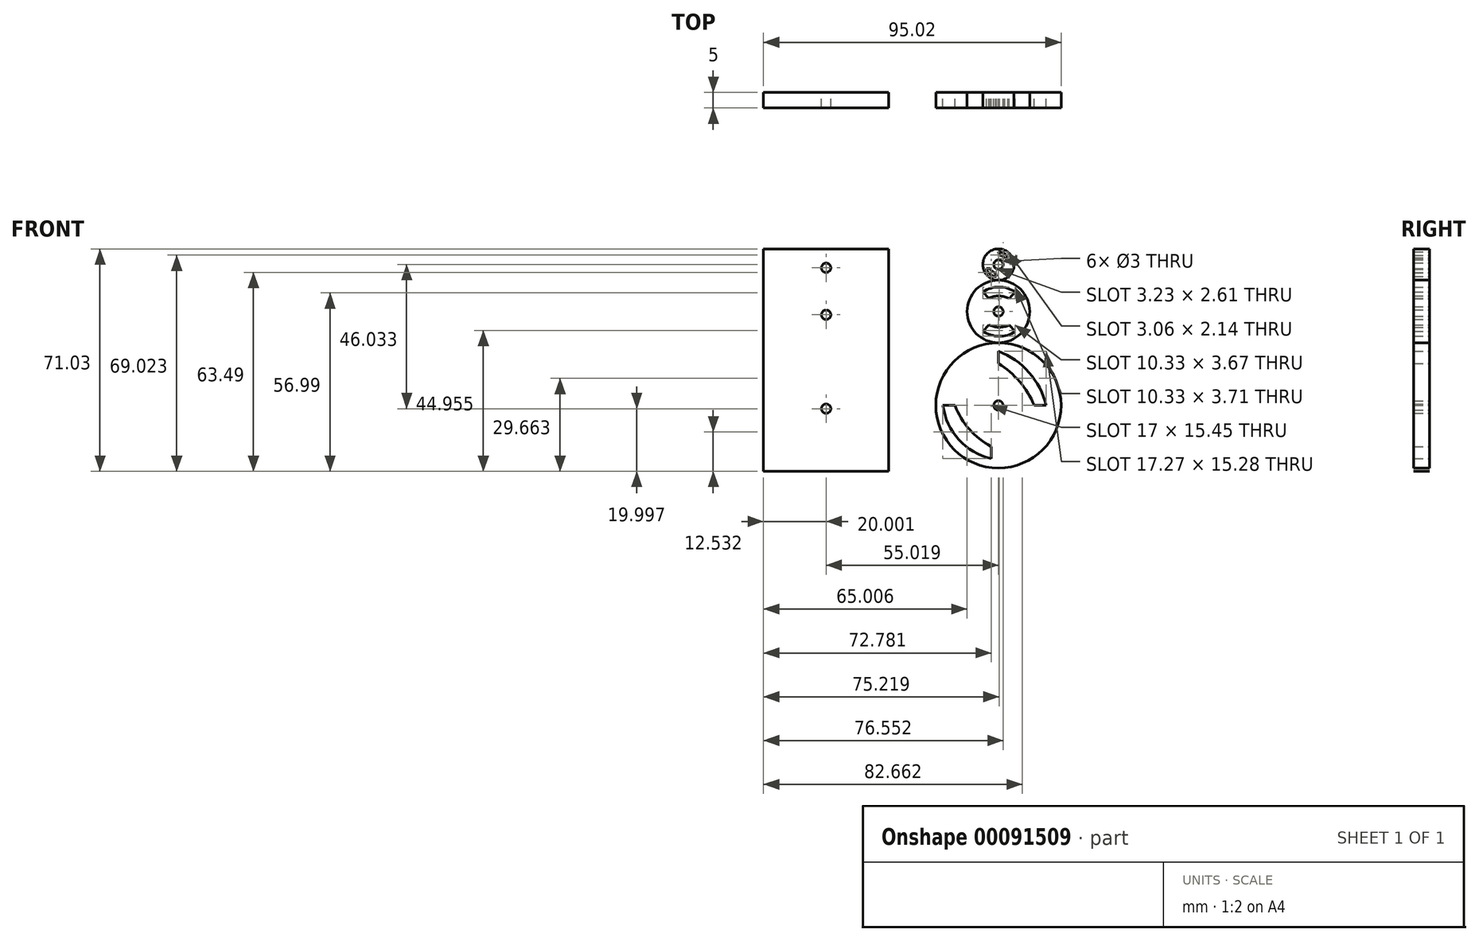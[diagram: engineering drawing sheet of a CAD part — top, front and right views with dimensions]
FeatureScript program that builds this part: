
annotation { "Feature Type Name" : "Feature", "Feature Type Description" : "" }
export const myFeature = defineFeature(function(context is Context, id is Id, definition is map)
    precondition{}
    {
        {
            var Q0;
            Q0=qCreatedBy(makeId("Front.planeOp"),FACE);
            var sketch = newSketch(context, id + "F0", { "sketchPlane" : qUnion([Q0])});
            skCircle(sketch, "E0", {"center": v(0, 0) * mm, "radius": 20 * mm});
            skCircle(sketch, "E1", {"center": v(0, 30) * mm, "radius": 10 * mm});
            skCircle(sketch, "E2", {"center": v(0, 0) * mm, "radius": 1.5 * mm});
            skCircle(sketch, "E3", {"center": v(0, 30) * mm, "radius": 1.5 * mm});
            skLineSegment(sketch, "E4", {"start": v(0, -20) * mm, "end": v(-20, -20) * mm});
            skLineSegment(sketch, "E5", {"start": v(0, -20) * mm, "end": v(20, -20) * mm});
            skCircle(sketch, "E6", {"center": v(0, 45) * mm, "radius": 5 * mm});
            skCircle(sketch, "E7", {"center": v(0, 45) * mm, "radius": 1.5 * mm});
            skLineSegment(sketch, "E8", {"start": v(20, -20) * mm, "end": v(20, 51) * mm});
            skLineSegment(sketch, "E9", {"start": v(20, 51) * mm, "end": v(20, 44.98) * mm});
            skLineSegment(sketch, "E10", {"start": v(-20, -20) * mm, "end": v(-20, 51) * mm});
            skLineSegment(sketch, "E11", {"start": v(-20, 51) * mm, "end": v(20, 51) * mm});
            skArc(sketch, "E12", {"start": v(-4.96, 23.72) * mm, "mid": v(0.18, 22.09) * mm, "end": v(5.36, 23.6) * mm});
            skLineSegment(sketch, "E13", {"start": v(-4.96, 23.72) * mm, "end": v(-3.01, 25.76) * mm});
            skLineSegment(sketch, "E14", {"start": v(5.36, 23.6) * mm, "end": v(3.44, 25.68) * mm});
            skArc(sketch, "E15", {"start": v(-3.01, 25.76) * mm, "mid": v(0.2, 24.98) * mm, "end": v(3.44, 25.68) * mm});
            skArc(sketch, "E16", {"start": v(5.36, 36.2) * mm, "mid": v(0.2, 37.82) * mm, "end": v(-4.96, 36.26) * mm});
            skLineSegment(sketch, "E17", {"start": v(-4.96, 36.26) * mm, "end": v(-3.01, 34.23) * mm});
            skLineSegment(sketch, "E18", {"start": v(5.36, 36.2) * mm, "end": v(3.44, 34.1) * mm});
            skArc(sketch, "E19", {"start": v(3.44, 34.1) * mm, "mid": v(0.23, 34.95) * mm, "end": v(-3.01, 34.23) * mm});
            skPoint(sketch, "E20.endSnap0", {"position": v(0.23, 34.95) * mm});
            skArc(sketch, "E21", {"start": v(-3.86, 43.76) * mm, "mid": v(-2.67, 41.92) * mm, "end": v(-0.62, 41.16) * mm});
            skLineSegment(sketch, "E22", {"start": v(-0.62, 41.16) * mm, "end": v(-0.89, 42.28) * mm});
            skLineSegment(sketch, "E23", {"start": v(-3.86, 43.76) * mm, "end": v(-2.7, 43.76) * mm});
            skArc(sketch, "E24", {"start": v(-2.7, 43.76) * mm, "mid": v(-1.96, 42.82) * mm, "end": v(-0.89, 42.28) * mm});
            skArc(sketch, "E25", {"start": v(3.06, 47.17) * mm, "mid": v(1.8, 48.56) * mm, "end": v(0, 49.06) * mm});
            skLineSegment(sketch, "E26", {"start": v(0, 49.06) * mm, "end": v(0.34, 47.97) * mm});
            skLineSegment(sketch, "E27", {"start": v(3.06, 47.17) * mm, "end": v(1.99, 46.92) * mm});
            skArc(sketch, "E28", {"start": v(1.99, 46.92) * mm, "mid": v(1.3, 47.65) * mm, "end": v(0.34, 47.97) * mm});
            skArc(sketch, "E29", {"start": v(-17.74, 0) * mm, "mid": v(-12.67, -10.91) * mm, "end": v(-2.3, -17) * mm});
            skLineSegment(sketch, "E30", {"start": v(-2.3, -17) * mm, "end": v(-2.3, -13.14) * mm});
            skLineSegment(sketch, "E31", {"start": v(-17.74, 0) * mm, "end": v(-13.88, 0) * mm});
            skArc(sketch, "E32", {"start": v(-13.88, 0) * mm, "mid": v(-9.28, -7.62) * mm, "end": v(-2.3, -13.14) * mm});
            skArc(sketch, "E33", {"start": v(15.28, 0) * mm, "mid": v(9.77, 10.52) * mm, "end": v(0, 17.27) * mm});
            skLineSegment(sketch, "E34", {"start": v(0, 17.27) * mm, "end": v(0, 13.4) * mm});
            skLineSegment(sketch, "E35", {"start": v(15.28, 0) * mm, "end": v(11.42, 0) * mm});
            skArc(sketch, "E36", {"start": v(11.42, 0) * mm, "mid": v(6.77, 7.6) * mm, "end": v(0, 13.4) * mm});
            skLineSegment(sketch, "E37", {"start": v(-75.02, 49.97) * mm, "end": v(-75.02, -21.03) * mm});
            skLineSegment(sketch, "E38", {"start": v(-75.02, -21.03) * mm, "end": v(-35.02, -21.03) * mm});
            skLineSegment(sketch, "E39", {"start": v(-35.02, -21.03) * mm, "end": v(-35.02, 49.97) * mm});
            skLineSegment(sketch, "E40", {"start": v(-75.02, 49.97) * mm, "end": v(-35.02, 49.97) * mm});
            skLineSegment(sketch, "E41", {"start": v(-55.02, -21.03) * mm, "end": v(-55.02, -1.03) * mm});
            skCircle(sketch, "E42", {"center": v(-55.02, -1.03) * mm, "radius": 1.5 * mm});
            skLineSegment(sketch, "E43", {"start": v(-55.02, -1.03) * mm, "end": v(-55.02, 28.97) * mm});
            skLineSegment(sketch, "E44", {"start": v(-55.02, 28.97) * mm, "end": v(-55.02, 43.97) * mm});
            skCircle(sketch, "E45", {"center": v(-55.02, 28.97) * mm, "radius": 1.5 * mm});
            skCircle(sketch, "E46", {"center": v(-55.02, 43.97) * mm, "radius": 1.5 * mm});
            skSolve(sketch);
        }
        {
            var Q0;
            Q0=makeQuery(id+"F0.imprint","IMPRINT",FACE,{"disambiguationData":[TD([[makeQuery(id+"F0.imprint","IMPRINT",EDGE,{"derivedFrom":sQuery(id+"F0.wireOp",EDGE,"E2")}),-1.0]])]});
            extrude(context, id + "F1", {"entities" : qUnion([Q0]), "depth" : 5 * mm});
        }
        {
            var Q0;
            Q0=makeQuery(id+"F0.imprint","IMPRINT",FACE,{"disambiguationData":[TD([[makeQuery(id+"F0.imprint","IMPRINT",EDGE,{"derivedFrom":sQuery(id+"F0.wireOp",EDGE,"E3")}),-1.0]])]});
            extrude(context, id + "F2", {"entities" : qUnion([Q0]), "operationType" : NewBodyOperationType.ADD, "depth" : 5 * mm});
        }
        {
            var Q0;
            Q0=makeQuery(id+"F0.imprint","IMPRINT",FACE,{"disambiguationData":[TD([[makeQuery(id+"F0.imprint","IMPRINT",EDGE,{"derivedFrom":sQuery(id+"F0.wireOp",EDGE,"E6")}),1.0]])]});
            extrude(context, id + "F3", {"entities" : qUnion([Q0]), "operationType" : NewBodyOperationType.ADD, "depth" : 5 * mm});
        }
        {
            var Q0;
            {var subQ7=sQuery(id+"F0.wireOp",EDGE,"E37");Q0=makeQuery(id+"F0.imprint","IMPRINT",FACE,{"disambiguationData":[TD([[makeQuery(id+"F0.imprint","IMPRINT",EDGE,{"derivedFrom":subQ7}),1.0]])]});}
            extrude(context, id + "F4", {"entities" : qUnion([Q0]), "depth" : 5 * mm});
        }
    });
